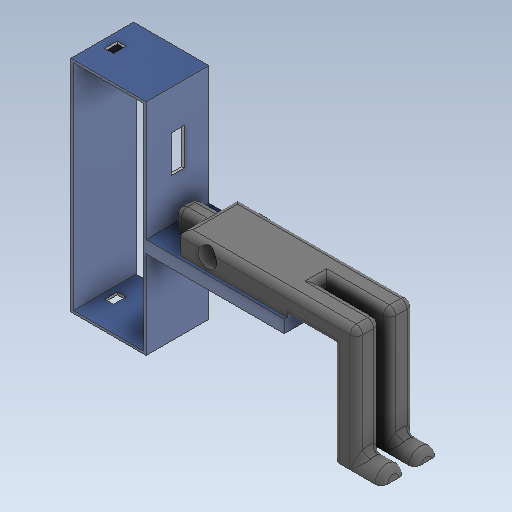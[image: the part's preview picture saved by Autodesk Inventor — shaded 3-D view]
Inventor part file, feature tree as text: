
AUTODESK INVENTOR PART (.ipt)
format: ipt  version: 2021 (Build 250183000, 183)  size: 360,448 bytes
history: native  units: mm
features: extrude x10, sketch x10, fillet x3
ambient origin geometry x8: Origin, YZ Plane, XZ Plane, XY Plane, X Axis, Y Axis, Z Axis, Center Point
bodies: Solid1 (feature_tree)
feature tree (23):
  extrude  "Extrusion1"  Depth=175.0mm
  extrude  "Extrusion9"  Depth=50.0mm TaperAngle=0.0deg
  extrude  "Extrusion10"  Depth=10.0mm
  extrude  "Extrusion11"  Depth=25.0mm
  extrude  "Extrusion12"  Depth=15.0mm
  fillet  "Fillet3"  Radius=21.57mm
  extrude  "Extrusion13"  Depth=90.0mm
  extrude  "Extrusion14"  Depth=17.0mm TaperAngle=0.0deg
  extrude  "Extrusion15"  Depth=50.0mm
  fillet  "Fillet4"  Radius=19.0mm
  fillet  "Fillet5"  Radius=50.0mm
  extrude  "Extrusion16"  Depth=80.0mm TaperAngle=0.0deg
  extrude  "Extrusion17"  Depth=20.3mm
  sketch  "Sketch1"  dims[d0=60.0mm d1=175.0mm]
  sketch  "Sketch9"  dims[d2=2.0mm d3=50.0mm d4=0.0mm]
  sketch  "Sketch10"  dims[d31=10.0mm d32=95.0mm]
  sketch  "Sketch11"  dims[d33=110.0mm d34=0.0mm d35=25.0mm]
  sketch  "Sketch12"  dims[d36=18.0mm d37=0.0mm d38=15.0mm d39=21.57mm]
  sketch  "Sketch14"  dims[d40=8.5mm d41=90.0mm]
  sketch  "Sketch15"  dims[d42=0.0mm d43=0.0mm d44=17.0mm d45=0.0mm]
  sketch  "Sketch16"  dims[d46=5.0mm d50=19.0mm d51=19.0mm d52=50.0mm d53=0.0mm]
  sketch  "Sketch17"  dims[d54=18.0mm d55=80.0mm d56=0.0mm]
  sketch  "Sketch18"  dims[d57=9.5mm d58=9.596734mm d59=20.0mm d60=0.0mm d61=5.0mm d62=5.0mm d63=10.0mm d64=31.43mm d65=60.87mm d66=20.3mm d67=5.0mm d68=0.0mm d69=7.0mm d70=10.0mm d71=46.33mm d72=20.3mm d73=0.0mm d74=0.0mm]
